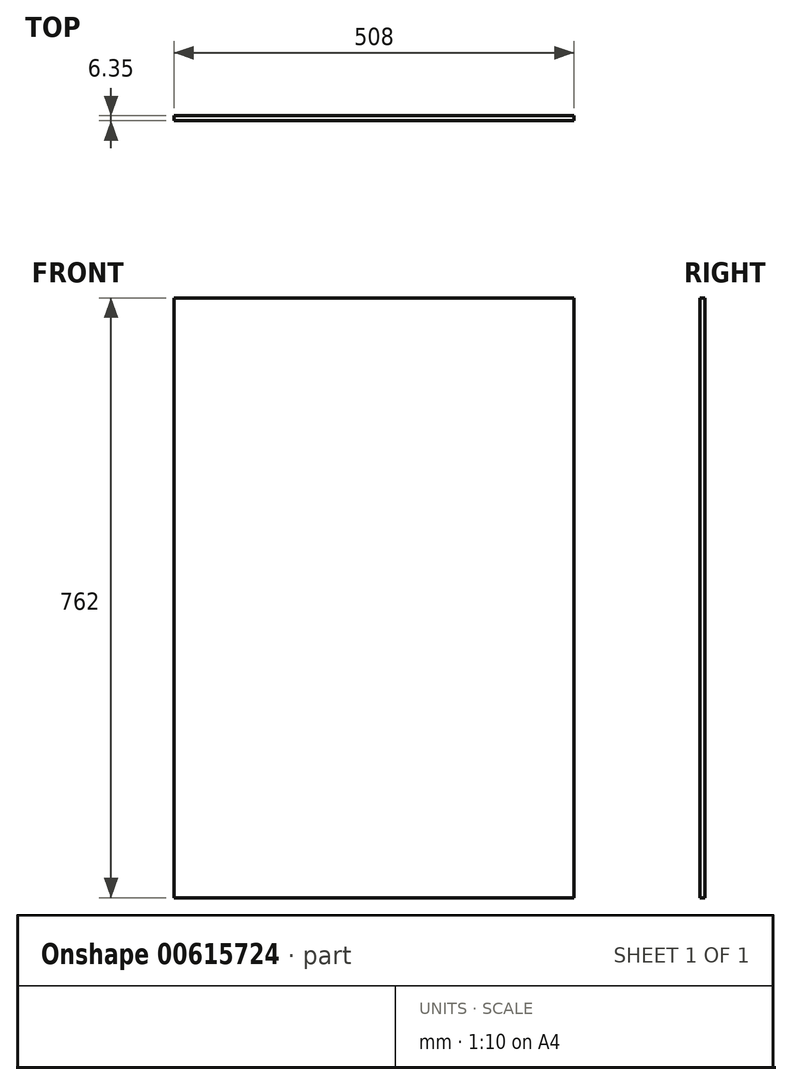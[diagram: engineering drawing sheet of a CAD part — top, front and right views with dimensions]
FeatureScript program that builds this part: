
annotation { "Feature Type Name" : "Feature", "Feature Type Description" : "" }
export const myFeature = defineFeature(function(context is Context, id is Id, definition is map)
    precondition{}
    {
        {
            var Q0;
            Q0=qCreatedBy(makeId("Front.planeOp"),FACE);
            var sketch = newSketch(context, id + "F0", { "sketchPlane" : qUnion([Q0])});
            skLineSegment(sketch, "E0.bottom", {"start": v(-210.88, 330.92) * mm, "end": v(297.12, 330.92) * mm});
            skLineSegment(sketch, "E0.top", {"start": v(-210.88, -431.08) * mm, "end": v(297.12, -431.08) * mm});
            skLineSegment(sketch, "E0.left", {"start": v(-210.88, 330.92) * mm, "end": v(-210.88, -431.08) * mm});
            skLineSegment(sketch, "E0.right", {"start": v(297.12, 330.92) * mm, "end": v(297.12, -431.08) * mm});
            skSolve(sketch);
        }
        {
            var Q0;
            Q0=makeQuery(id+"F0.imprint","IMPRINT",FACE,{"disambiguationData":[TD([[makeQuery(id+"F0.imprint","IMPRINT",EDGE,{"derivedFrom":sQuery(id+"F0.wireOp",EDGE,"E0.bottom")}),-1.0]])]});
            extrude(context, id + "F1", {"entities" : qUnion([Q0]), "depth" : 6.35 * mm, "offsetDistance" : 25.4 * mm});
        }
    });
